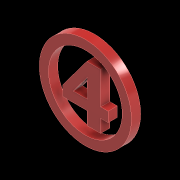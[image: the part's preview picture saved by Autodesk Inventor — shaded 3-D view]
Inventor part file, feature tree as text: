
AUTODESK INVENTOR PART (.ipt)
format: ipt  version: 2020 (Build 240168000, 168)  size: 142,848 bytes
history: native  units: mm
features: other x5, extrude x2, sketch x2
ambient origin geometry x8: Origin, YZ Plane, XZ Plane, XY Plane, X Axis, Y Axis, Z Axis, Center Point
bodies: Body1 (feature_tree)
feature tree (9):
  other  "自動販賣機.ipt"
  extrude  "擠出1"  Depth=10.0mm
  extrude  "擠出2"  Depth=10.0mm TaperAngle=0.0deg
  other  "實體49::自動販賣機.ipt"
  other  "標籤特徵1"
  sketch  "草圖1"
  sketch  "草圖2"
  other  "實體1"
  other  "投影切割邊1"
